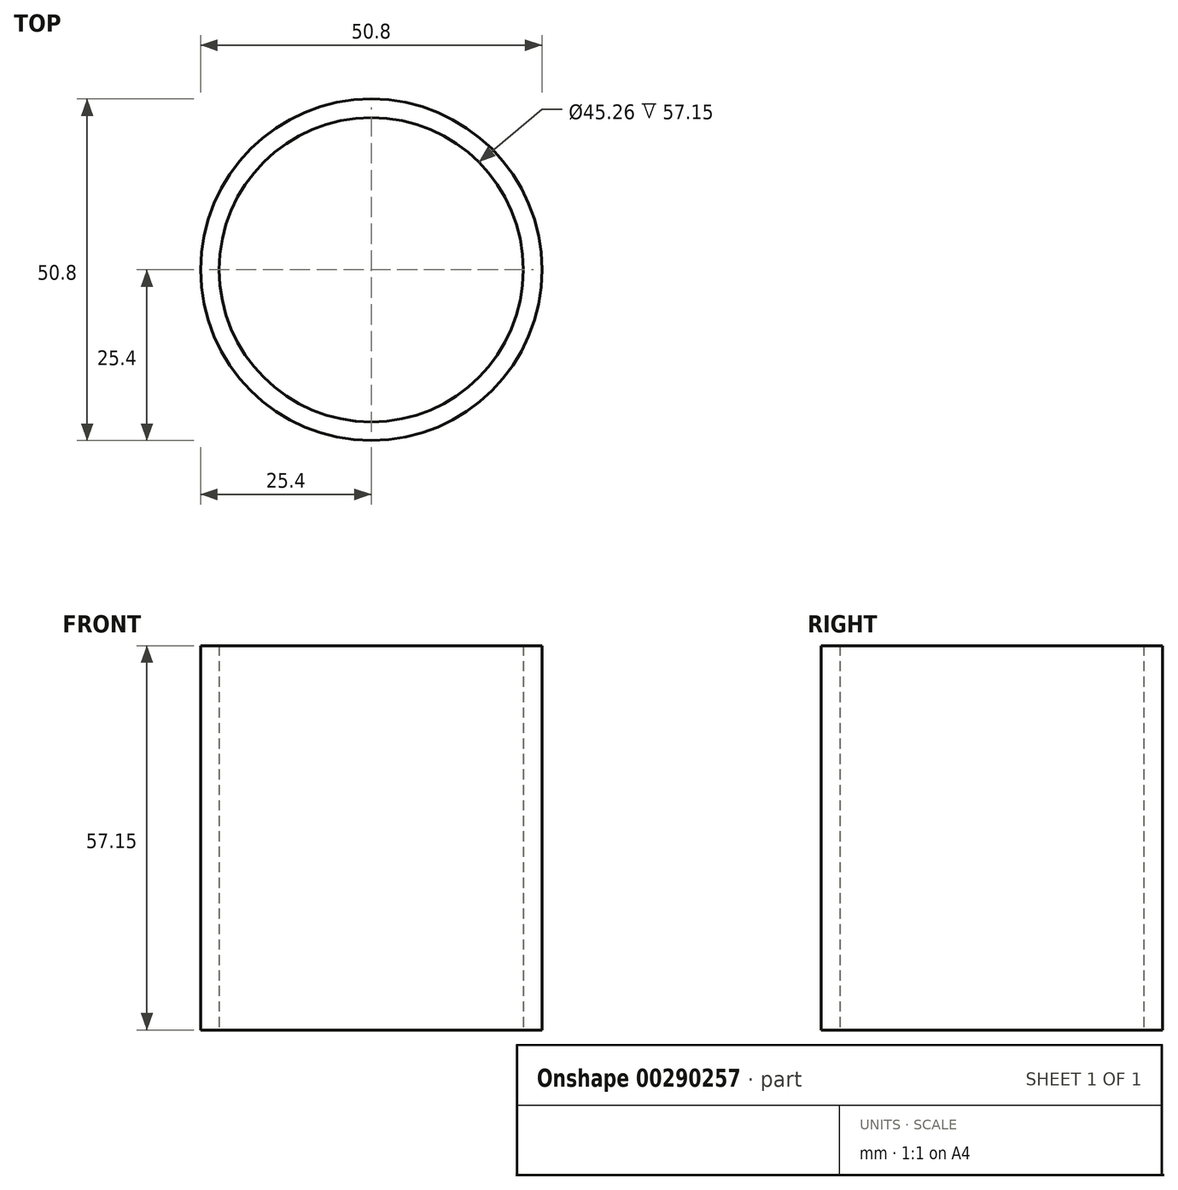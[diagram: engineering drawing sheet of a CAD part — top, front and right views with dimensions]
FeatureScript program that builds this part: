
annotation { "Feature Type Name" : "Feature", "Feature Type Description" : "" }
export const myFeature = defineFeature(function(context is Context, id is Id, definition is map)
    precondition{}
    {
        {
            var Q0;
            Q0=qCreatedBy(makeId("Top.planeOp"),FACE);
            var sketch = newSketch(context, id + "F0", { "sketchPlane" : qUnion([Q0])});
            skCircle(sketch, "E0", {"center": v(0, 0) * mm, "radius": 25.4 * mm});
            skCircle(sketch, "E1", {"center": v(0, 0) * mm, "radius": 22.63 * mm});
            skSolve(sketch);
        }
        {
            var Q0;
            Q0 = qSketchRegion(id + "F0", true);
            extrude(context, id + "F1", {"entities" : qUnion([Q0]), "depth" : 57.15 * mm});
        }
    });
